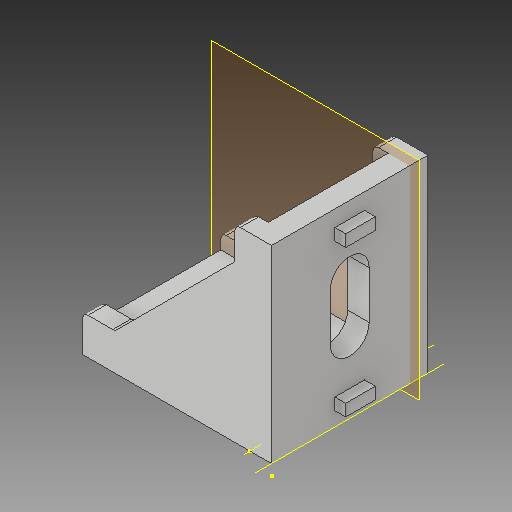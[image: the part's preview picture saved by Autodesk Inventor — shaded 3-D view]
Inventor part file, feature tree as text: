
AUTODESK INVENTOR PART (.ipt)
format: ipt  version: 2018 (Build 220112000, 112)  size: 187,392 bytes
history: native  units: mm
features: sketch x8, other x5, plane x1
ambient origin geometry x8: Origin, YZ Plane, XZ Plane, XY Plane, X Axis, Y Axis, Z Axis, Center Point
bodies: Solid1 (feature_tree)
feature tree (14):
  other  "30mm Bracket_CPY_MIR2_MIR1.ipt"
  other  "Solid1::30mm Bracket_CPY_MIR2_MIR1.ipt"
  other  "TaggingFeature1"
  sketch  "Sketch1"  dims[d0=10.0mm]
  sketch  "Sketch2"
  sketch  "Sketch3"
  sketch  "Sketch4"
  sketch  "Sketch5"
  sketch  "Sketch7"
  sketch  "Sketch9"
  sketch  "Sketch10"
  plane  "Work Plane1"
  other  "Work Axis1"
  other  "Work Axis2"
